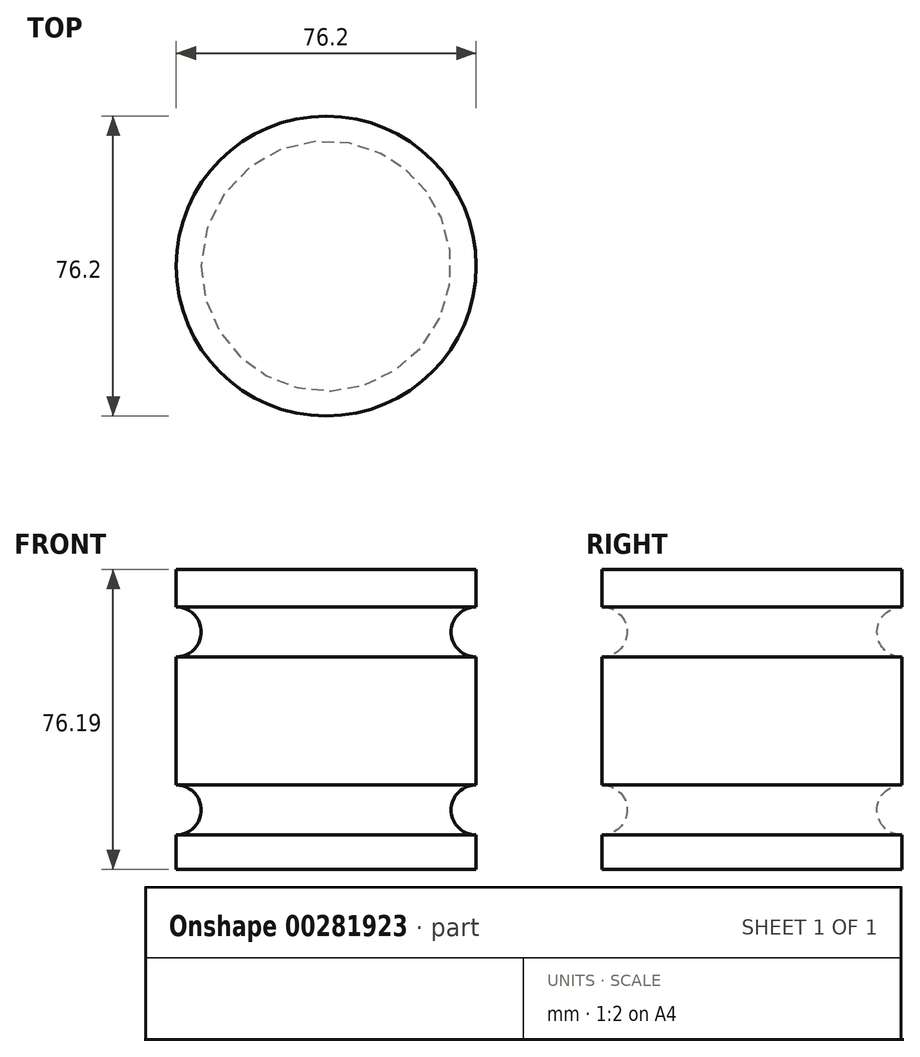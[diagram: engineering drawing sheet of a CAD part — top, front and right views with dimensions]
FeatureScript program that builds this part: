
annotation { "Feature Type Name" : "Feature", "Feature Type Description" : "" }
export const myFeature = defineFeature(function(context is Context, id is Id, definition is map)
    precondition{}
    {
        {
            var Q0;
            Q0=qCreatedBy(makeId("Front.planeOp"),FACE);
            var sketch = newSketch(context, id + "F0", { "sketchPlane" : qUnion([Q0])});
            skLineSegment(sketch, "E0.bottom", {"start": v(0, 0) * mm, "end": v(-38.1, 0) * mm});
            skLineSegment(sketch, "E0.top", {"start": v(0, 76.2) * mm, "end": v(-38.1, 76.2) * mm});
            skLineSegment(sketch, "E0.left", {"start": v(0, 0) * mm, "end": v(0, 8.74) * mm});
            skLineSegment(sketch, "E0.right", {"start": v(-38.1, 0) * mm, "end": v(-38.1, 76.2) * mm});
            skArc(sketch, "E1", {"start": v(0, 66.7) * mm, "mid": v(-6.35, 60.34) * mm, "end": v(0, 54) * mm});
            skArc(sketch, "E2", {"start": v(0, 21.44) * mm, "mid": v(-6.35, 15.09) * mm, "end": v(0, 8.74) * mm});
            skLineSegment(sketch, "E3.trimOffspring", {"start": v(0, 66.7) * mm, "end": v(0, 76.2) * mm});
            skLineSegment(sketch, "E4.trimOffspring", {"start": v(0, 21.44) * mm, "end": v(0, 54) * mm});
            skSolve(sketch);
        }
        {
            var Q0;
            Q0=makeQuery(id+"F0.imprint","IMPRINT",FACE,{"disambiguationData":[TD([[makeQuery(id+"F0.imprint","IMPRINT",EDGE,{"derivedFrom":sQuery(id+"F0.wireOp",EDGE,"E0.bottom")}),-1.0]])]});
            var Q1;
            Q1=sQuery(id+"F0.wireOp",EDGE,"E0.right");
            revolve(context, id + "F1", {"entities" : qUnion([Q0]), "axis" : qUnion([Q1]), "revolveType" : RevolveType.FULL});
        }
    });
